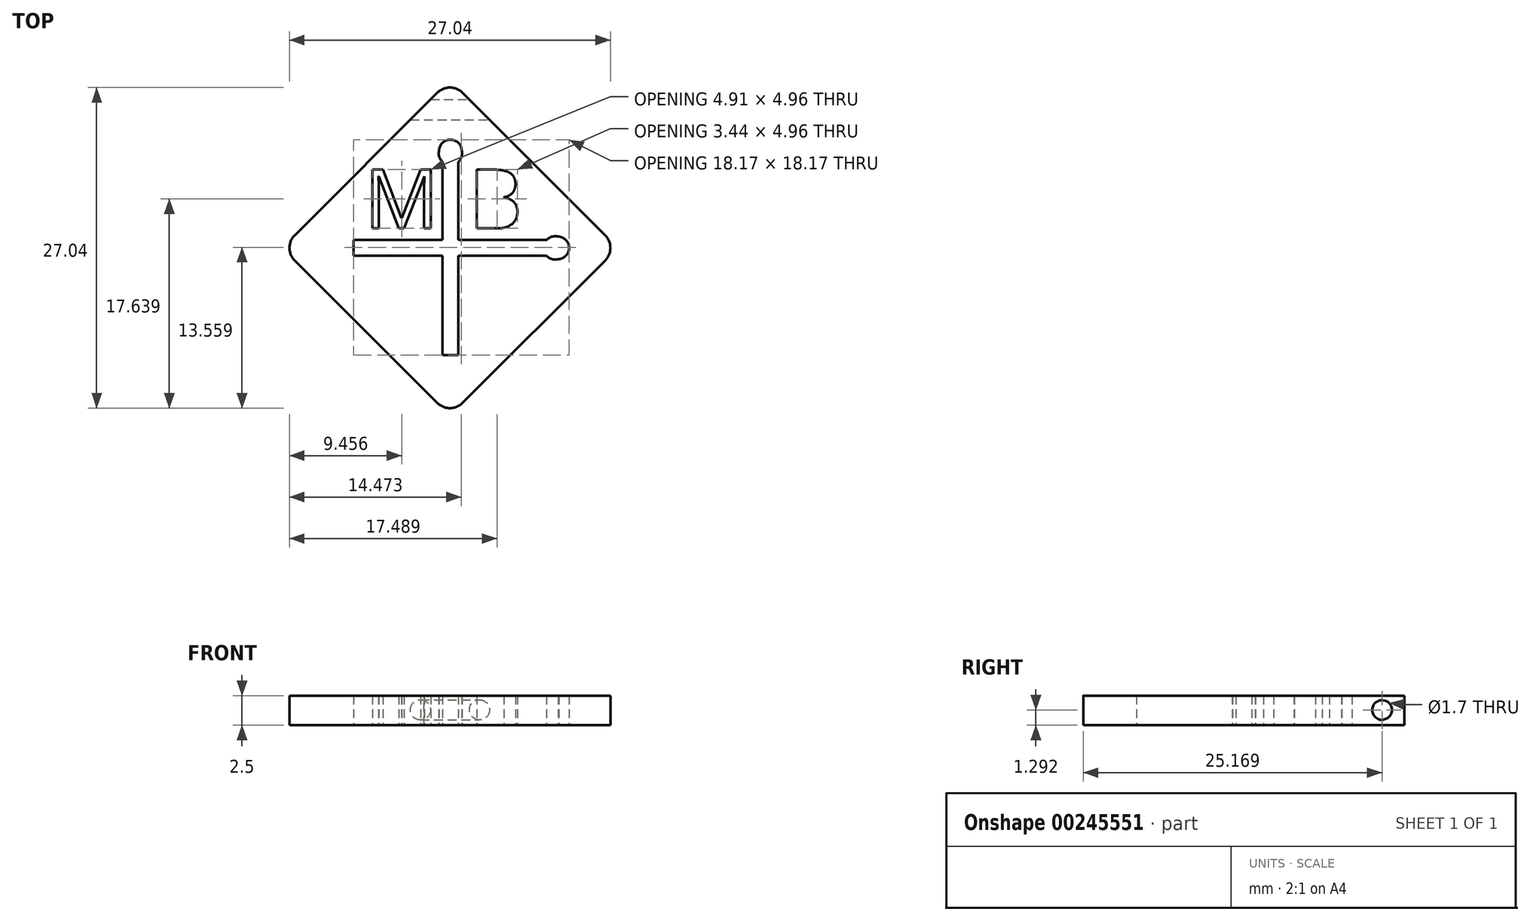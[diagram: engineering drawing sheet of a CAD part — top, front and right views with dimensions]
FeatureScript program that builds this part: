
annotation { "Feature Type Name" : "Feature", "Feature Type Description" : "" }
export const myFeature = defineFeature(function(context is Context, id is Id, definition is map)
    precondition{}
    {
        {
            var Q0;
            Q0=qCreatedBy(makeId("Top.planeOp"),FACE);
            var sketch = newSketch(context, id + "F0", { "sketchPlane" : qUnion([Q0])});
            skLineSegment(sketch, "E0", {"start": v(1.06, -1.06) * mm, "end": v(13.08, -13.08) * mm});
            skLineSegment(sketch, "E1", {"start": v(13.08, -15.2) * mm, "end": v(1.06, -27.22) * mm});
            skLineSegment(sketch, "E2", {"start": v(-1.06, -27.22) * mm, "end": v(-13.08, -15.2) * mm});
            skLineSegment(sketch, "E3", {"start": v(-13.08, -13.08) * mm, "end": v(-1.06, -1.06) * mm});
            skPoint(sketch, "E4.visualSharp", {"position": v(0, 0) * mm});
            skArc(sketch, "E4.filletArc", {"start": v(1.06, -1.06) * mm, "mid": v(0, -0.62) * mm, "end": v(-1.06, -1.06) * mm});
            skPoint(sketch, "E5.visualSharp", {"position": v(-14.14, -14.14) * mm});
            skArc(sketch, "E5.filletArc", {"start": v(-13.08, -13.08) * mm, "mid": v(-13.52, -14.14) * mm, "end": v(-13.08, -15.2) * mm});
            skPoint(sketch, "E6.visualSharp", {"position": v(14.14, -14.14) * mm});
            skArc(sketch, "E6.filletArc", {"start": v(13.08, -15.2) * mm, "mid": v(13.52, -14.14) * mm, "end": v(13.08, -13.08) * mm});
            skPoint(sketch, "E7.visualSharp", {"position": v(0, -28.28) * mm});
            skArc(sketch, "E7.filletArc", {"start": v(-1.06, -27.22) * mm, "mid": v(0, -27.66) * mm, "end": v(1.06, -27.22) * mm});
            skLineSegment(sketch, "E8", {"start": v(0, 0) * mm, "end": v(0, -31.86) * mm, "construction": true});
            skLineSegment(sketch, "E9", {"start": v(-14.14, -14.14) * mm, "end": v(14.14, -14.14) * mm, "construction": true});
            skLineSegment(sketch, "E10", {"start": v(-8.13, -13.48) * mm, "end": v(-8.13, -14.8) * mm});
            skLineSegment(sketch, "E11", {"start": v(-8.13, -14.8) * mm, "end": v(8.13, -14.8) * mm});
            skLineSegment(sketch, "E12", {"start": v(8.13, -13.48) * mm, "end": v(-8.13, -13.48) * mm});
            skLineSegment(sketch, "E13", {"start": v(-8.13, -13.48) * mm, "end": v(0, -13.48) * mm, "construction": true});
            skLineSegment(sketch, "E14", {"start": v(0, -13.48) * mm, "end": v(8.13, -13.48) * mm, "construction": true});
            skArc(sketch, "E15", {"start": v(9.18, -15.1) * mm, "mid": v(10.04, -14.12) * mm, "end": v(9.13, -13.2) * mm});
            skArc(sketch, "E16", {"start": v(9.13, -13.2) * mm, "mid": v(8.6, -13.2) * mm, "end": v(8.13, -13.48) * mm});
            skArc(sketch, "E17", {"start": v(8.13, -14.8) * mm, "mid": v(8.61, -15.1) * mm, "end": v(9.18, -15.1) * mm});
            skLineSegment(sketch, "E18", {"start": v(-0.62, -23.19) * mm, "end": v(0.7, -23.19) * mm});
            skLineSegment(sketch, "E19", {"start": v(0.7, -23.19) * mm, "end": v(0.7, -6.92) * mm});
            skLineSegment(sketch, "E20", {"start": v(-0.62, -6.92) * mm, "end": v(-0.62, -23.19) * mm});
            skLineSegment(sketch, "E21", {"start": v(-0.62, -23.19) * mm, "end": v(-0.62, -15.05) * mm, "construction": true});
            skLineSegment(sketch, "E22", {"start": v(-0.62, -15.05) * mm, "end": v(-0.62, -6.92) * mm, "construction": true});
            skArc(sketch, "E23", {"start": v(0.99, -5.88) * mm, "mid": v(0.02, -5.01) * mm, "end": v(-0.91, -5.92) * mm});
            skArc(sketch, "E24", {"start": v(-0.91, -5.92) * mm, "mid": v(-0.9, -6.46) * mm, "end": v(-0.62, -6.92) * mm});
            skArc(sketch, "E25", {"start": v(0.7, -6.92) * mm, "mid": v(1, -6.44) * mm, "end": v(0.99, -5.88) * mm});
            skText(sketch, "E26", { "text": "M", "fontName": "OpenSans-Regular.ttf"});
            skText(sketch, "E27", { "text": "B\n", "fontName": "OpenSans-Regular.ttf"});
            const initialGuessF0  = {"E26": [-0.0072, -0.0125, 1, 0, 0.005], "E27": [0.00157, -0.0125, 1, 0, 0.005]};
            skSetInitialGuess(sketch, initialGuessF0);
            skSolve(sketch);
        }
        {
            var Q0;
            Q0=makeQuery(id+"F0.imprint","IMPRINT",FACE,{"disambiguationData":[TD([[makeQuery(id+"F0.imprint","IMPRINT",EDGE,{"derivedFrom":sQuery(id+"F0.wireOp",EDGE,"E0")}),-1.0]])]});
            extrude(context, id + "F1", {"entities" : qUnion([Q0]), "depth" : 2.5 * mm});
        }
        {
            var Q0;
            Q0=qCreatedBy(makeId("Right.planeOp"),FACE);
            var sketch = newSketch(context, id + "F2", { "sketchPlane" : qUnion([Q0])});
            skCircle(sketch, "E28", {"center": v(-2.5, 1.3) * mm, "radius": 0.85 * mm});
            skSolve(sketch);
        }
        {
            var Q0;
            Q0 = qSketchRegion(id + "F2", true);
            extrude(context, id + "F3", {"entities" : qUnion([Q0]), "operationType" : NewBodyOperationType.REMOVE, "endBound" : BoundingType.SYMMETRIC, "oppositeDirection" : true, "depth" : 25 * mm});
        }
    });
